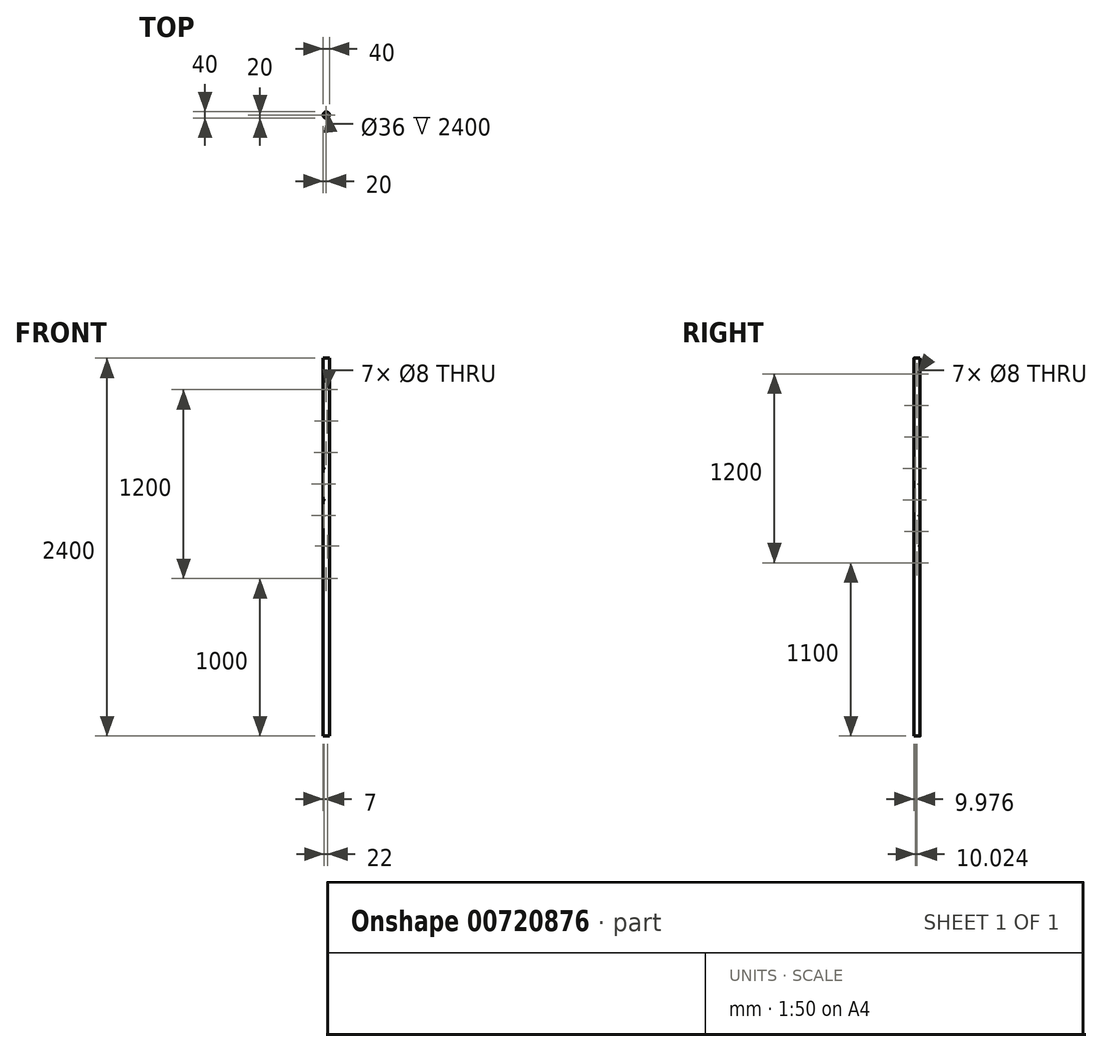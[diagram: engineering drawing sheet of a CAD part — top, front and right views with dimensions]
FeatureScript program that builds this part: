
annotation { "Feature Type Name" : "Feature", "Feature Type Description" : "" }
export const myFeature = defineFeature(function(context is Context, id is Id, definition is map)
    precondition{}
    {
        {
            var Q0;
            Q0=qCreatedBy(makeId("Top.planeOp"),FACE);
            var sketch = newSketch(context, id + "F0", { "sketchPlane" : qUnion([Q0])});
            skCircle(sketch, "E0", {"center": v(0, 0) * mm, "radius": 20 * mm});
            skCircle(sketch, "E1.0", {"center": v(0, 0) * mm, "radius": 18 * mm});
            skSolve(sketch);
        }
        {
            var Q0;
            Q0=makeQuery(id+"F0.imprint","IMPRINT",FACE,{"disambiguationData":[TD([[makeQuery(id+"F0.imprint","IMPRINT",EDGE,{"derivedFrom":sQuery(id+"F0.wireOp",EDGE,"E0")}),1.0]])]});
            extrude(context, id + "F1", {"entities" : qUnion([Q0]), "depth" : 2400 * mm, "offsetDistance" : 25 * mm});
        }
        {
            var Q0;
            Q0=qCreatedBy(makeId("Front.planeOp"),FACE);
            var sketch = newSketch(context, id + "F2", { "sketchPlane" : qUnion([Q0])});
            skPoint(sketch, "E2", {"position": v(0, 1000) * mm});
            skPoint(sketch, "E3.0.2.0", {"position": v(9, 1206.22) * mm});
            skPoint(sketch, "E3.0.4.0", {"position": v(-13, 1400) * mm});
            skPoint(sketch, "E3.0.6.0", {"position": v(-13, 1600) * mm});
            skPoint(sketch, "E3.0.8.0", {"position": v(0, 1800) * mm});
            skPoint(sketch, "E3.0.10.0", {"position": v(5, 2000) * mm});
            skPoint(sketch, "E3.0.11.0", {"position": v(0, 2100) * mm});
            skPoint(sketch, "E3.0.12.0", {"position": v(0, 2200) * mm});
            skLineSegment(sketch, "E3.direction1", {"start": v(0, 1000) * mm, "end": v(69.1, 1000) * mm, "construction": true});
            skLineSegment(sketch, "E3.direction2", {"start": v(0, 1000) * mm, "end": v(0, 1100) * mm, "construction": true});
            skPoint(sketch, "E4.0.0.13", {"position": v(-5.84, 2300) * mm});
            skSolve(sketch);
        }
        {
            var Q0;
            Q0=sQuery(id+"F2.wireOp",VERTEX,"E3.0.8.0");
            var Q1;
            Q1=sQuery(id+"F2.wireOp",VERTEX,"E3.0.5.0");
            var Q2;
            Q2=sQuery(id+"F2.wireOp",VERTEX,"E3.0.2.0");
            var Q3;
            Q3=sQuery(id+"F2.wireOp",VERTEX,"E2");
            var Q4;
            Q4=sQuery(id+"F2.wireOp",VERTEX,"E3.0.1.0");
            var Q5;
            Q5=sQuery(id+"F2.wireOp",VERTEX,"E3.0.4.0");
            var Q6;
            Q6=sQuery(id+"F2.wireOp",VERTEX,"E3.0.3.0");
            var Q7;
            Q7=sQuery(id+"F2.wireOp",VERTEX,"E3.0.7.0");
            var Q8;
            Q8=sQuery(id+"F2.wireOp",VERTEX,"E3.0.9.0");
            var Q9;
            Q9=sQuery(id+"F2.wireOp",VERTEX,"E3.0.12.0");
            var Q10;
            Q10=sQuery(id+"F2.wireOp",VERTEX,"E3.0.6.0");
            var Q11;
            Q11=sQuery(id+"F2.wireOp",VERTEX,"E3.0.10.0");
            var Q12;
            Q12=makeQuery(id+"F1.opExtrude","SWEPT_BODY",BODY,{"disambiguationData":[OSD([sQuery(id+"F0.wireOp",EDGE,"E0"),sQuery(id+"F0.wireOp",EDGE,"E1.0")])]});
            hole(context, id + "F3", {"style" : HoleStyle.SIMPLE, "endStyle" : HoleEndStyle.THROUGH, "holeDiameter" : 8 * mm, "majorDiameter" : 5 * mm, "isTappedThrough" : true, "tappedDepth" : 12 * mm, "tapClearance" : 3, "locations" : qUnion([Q0, Q1, Q2, Q3, Q4, Q5, Q6, Q7, Q8, Q9, Q10, Q11]), "scope" : qUnion([Q12])});
        }
        {
            var Q0;
            Q0=qCreatedBy(makeId("Right.planeOp"),FACE);
            var sketch = newSketch(context, id + "F4", { "sketchPlane" : qUnion([Q0])});
            skPoint(sketch, "E5", {"position": v(0, 1100) * mm});
            skPoint(sketch, "E6.0.1.0", {"position": v(0, 1300) * mm});
            skPoint(sketch, "E6.0.2.0", {"position": v(-10.02, 1501) * mm});
            skPoint(sketch, "E6.0.3.0", {"position": v(-10.02, 1701) * mm});
            skPoint(sketch, "E6.0.4.0", {"position": v(0, 1900) * mm});
            skPoint(sketch, "E6.0.5.0", {"position": v(0, 2100) * mm});
            skPoint(sketch, "E6.0.6.0", {"position": v(0, 2300) * mm});
            skLineSegment(sketch, "E6.direction1", {"start": v(0, 1100) * mm, "end": v(25, 1100) * mm, "construction": true});
            skLineSegment(sketch, "E6.direction2", {"start": v(0, 1100) * mm, "end": v(0, 1300) * mm, "construction": true});
            skSolve(sketch);
        }
        {
            var Q0;
            Q0=sQuery(id+"F4.wireOp",VERTEX,"E6.0.2.0");
            var Q1;
            Q1=sQuery(id+"F4.wireOp",VERTEX,"E5");
            var Q2;
            Q2=sQuery(id+"F4.wireOp",VERTEX,"E6.0.1.0");
            var Q3;
            Q3=sQuery(id+"F4.wireOp",VERTEX,"E6.0.4.0");
            var Q4;
            Q4=sQuery(id+"F4.wireOp",VERTEX,"E6.0.3.0");
            var Q5;
            Q5=sQuery(id+"F4.wireOp",VERTEX,"E6.0.6.0");
            var Q6;
            Q6=sQuery(id+"F4.wireOp",VERTEX,"E6.0.5.0");
            var Q7;
            Q7=makeQuery(id+"F1.opExtrude","SWEPT_BODY",BODY,{"disambiguationData":[OSD([sQuery(id+"F0.wireOp",EDGE,"E0"),sQuery(id+"F0.wireOp",EDGE,"E1.0")])]});
            hole(context, id + "F5", {"style" : HoleStyle.SIMPLE, "endStyle" : HoleEndStyle.THROUGH, "holeDiameter" : 8 * mm, "majorDiameter" : 5 * mm, "isTappedThrough" : true, "tappedDepth" : 12 * mm, "tapClearance" : 3, "locations" : qUnion([Q0, Q1, Q2, Q3, Q4, Q5, Q6]), "scope" : qUnion([Q7])});
        }
    });
